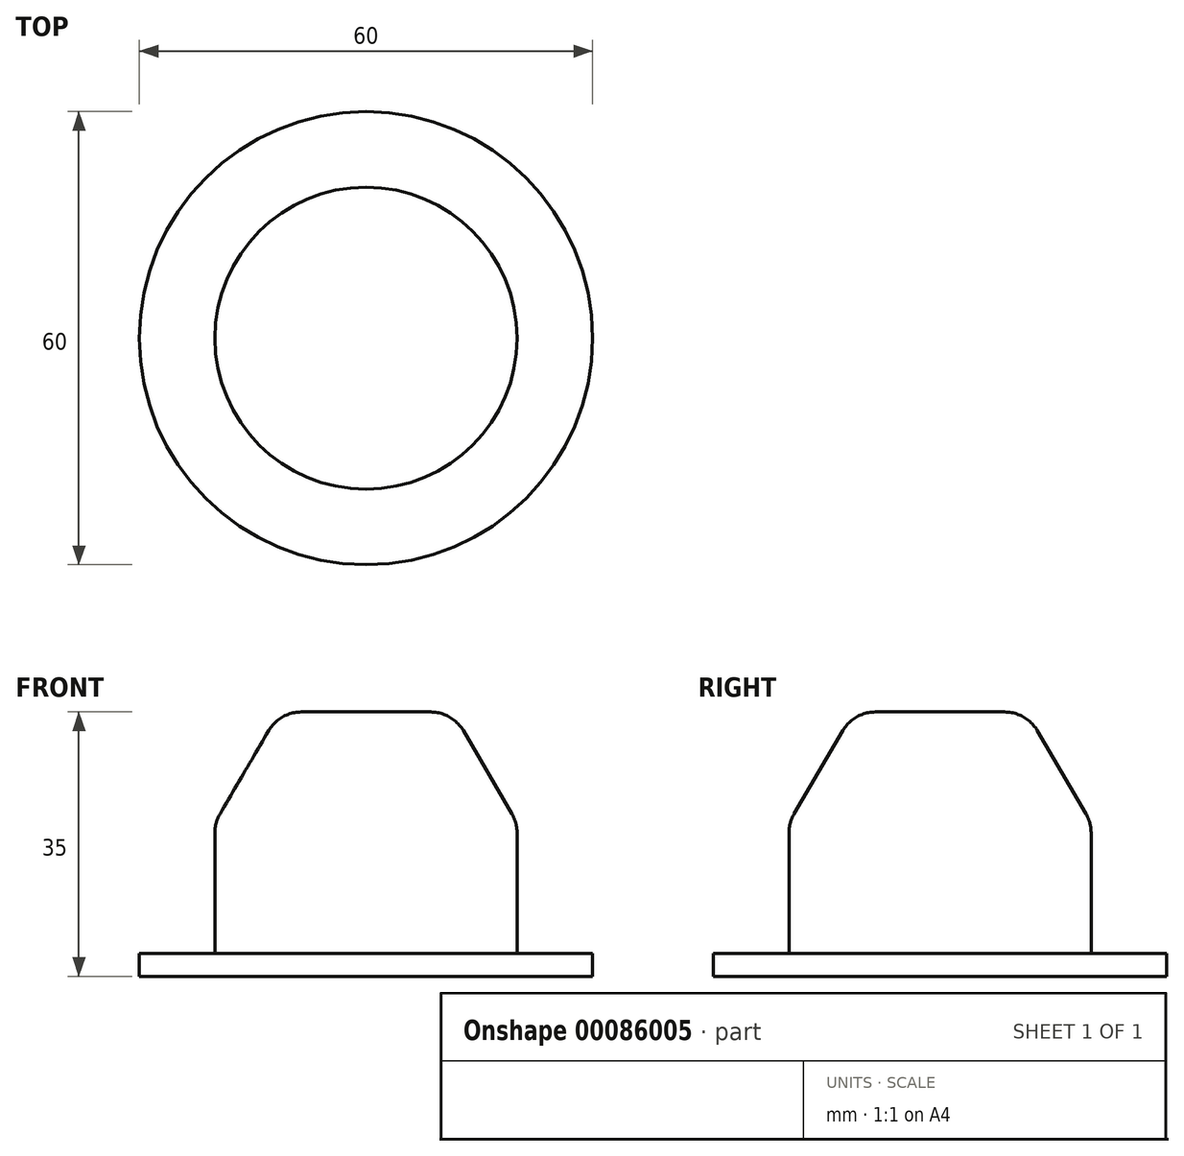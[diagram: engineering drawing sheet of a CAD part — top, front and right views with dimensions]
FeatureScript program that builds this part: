
annotation { "Feature Type Name" : "Feature", "Feature Type Description" : "" }
export const myFeature = defineFeature(function(context is Context, id is Id, definition is map)
    precondition{}
    {
        {
            var Q0;
            Q0=qCreatedBy(makeId("Front.planeOp"),FACE);
            var sketch = newSketch(context, id + "F0", { "sketchPlane" : qUnion([Q0])});
            skLineSegment(sketch, "E0", {"start": v(0, 0) * mm, "end": v(0, 35) * mm});
            skLineSegment(sketch, "E1", {"start": v(0, 35) * mm, "end": v(8.57, 35) * mm});
            skLineSegment(sketch, "E2", {"start": v(12.88, 32.52) * mm, "end": v(19.32, 21.52) * mm});
            skLineSegment(sketch, "E3", {"start": v(20, 19) * mm, "end": v(20, 3) * mm});
            skLineSegment(sketch, "E4", {"start": v(20, 3) * mm, "end": v(30, 3) * mm});
            skLineSegment(sketch, "E5", {"start": v(30, 3) * mm, "end": v(30, 0) * mm});
            skLineSegment(sketch, "E6", {"start": v(30, 0) * mm, "end": v(0, 0) * mm});
            skPoint(sketch, "E7.visualSharp", {"position": v(11.43, 35) * mm});
            skArc(sketch, "E7.filletArc", {"start": v(12.88, 32.52) * mm, "mid": v(11.05, 34.34) * mm, "end": v(8.57, 35) * mm});
            skPoint(sketch, "E8.visualSharp", {"position": v(20, 20.35) * mm});
            skArc(sketch, "E8.filletArc", {"start": v(20, 19) * mm, "mid": v(19.83, 20.3) * mm, "end": v(19.32, 21.52) * mm});
            skSolve(sketch);
        }
        {
            var Q0;
            Q0=makeQuery(id+"F0.imprint","IMPRINT",FACE,{"disambiguationData":[TD([[makeQuery(id+"F0.imprint","IMPRINT",EDGE,{"derivedFrom":sQuery(id+"F0.wireOp",EDGE,"E0")}),-1.0]])]});
            var Q1;
            Q1=sQuery(id+"F0.wireOp",EDGE,"E0");
            revolve(context, id + "F1", {"entities" : qUnion([Q0]), "axis" : qUnion([Q1]), "revolveType" : RevolveType.FULL});
        }
    });
